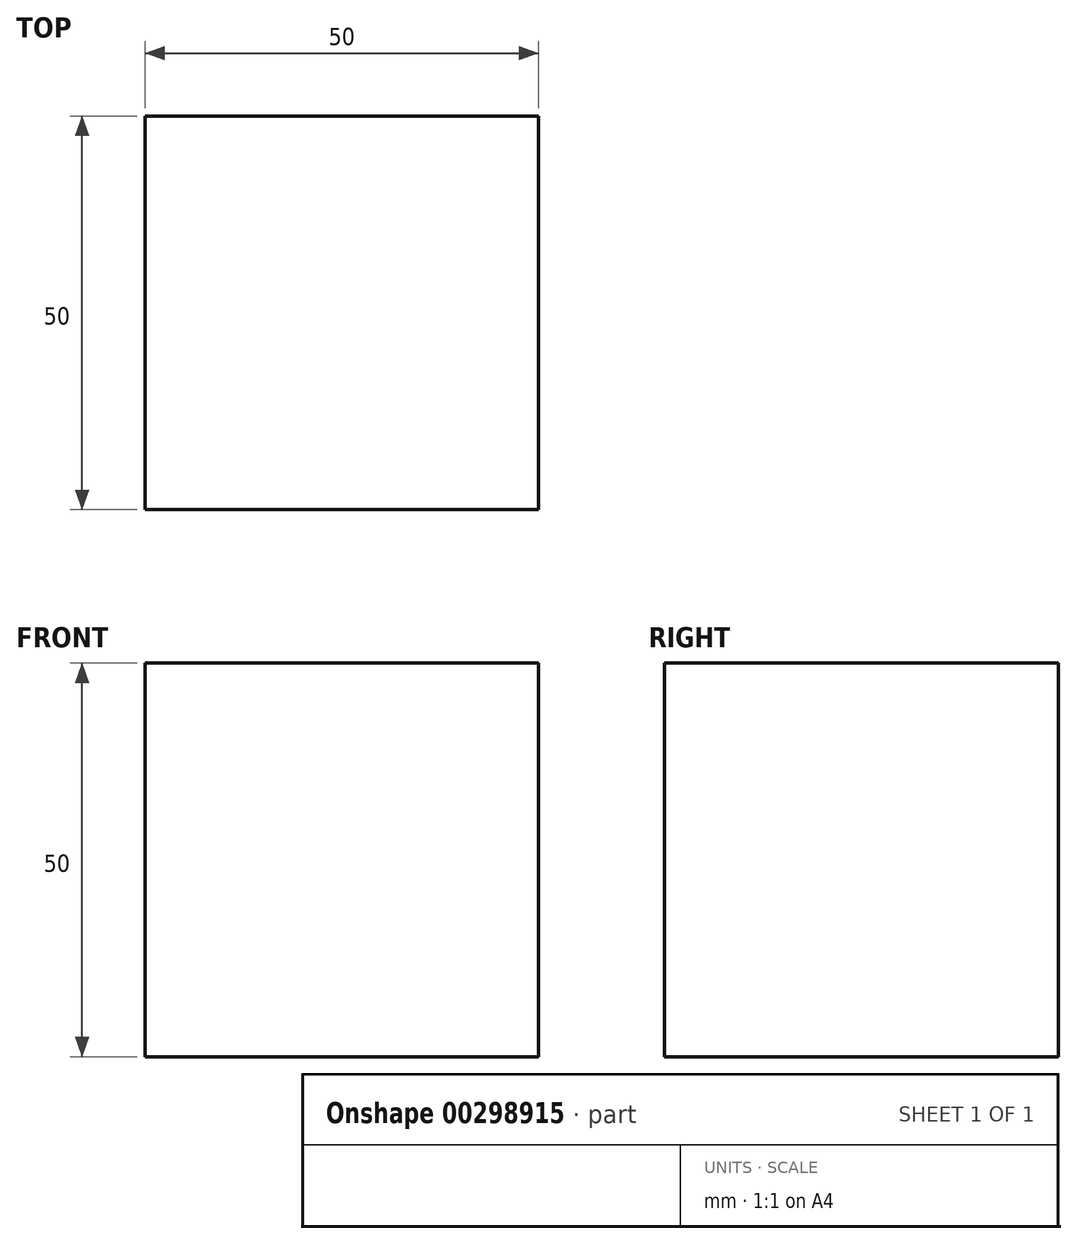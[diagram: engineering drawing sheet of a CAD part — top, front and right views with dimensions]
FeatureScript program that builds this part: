
annotation { "Feature Type Name" : "Feature", "Feature Type Description" : "" }
export const myFeature = defineFeature(function(context is Context, id is Id, definition is map)
    precondition{}
    {
        {
            var Q0;
            Q0=qCreatedBy(makeId("Top.planeOp"),FACE);
            var sketch = newSketch(context, id + "F0", { "sketchPlane" : qUnion([Q0])});
            skLineSegment(sketch, "E0.bottom", {"start": v(25, 25) * mm, "end": v(-25, 25) * mm});
            skLineSegment(sketch, "E0.top", {"start": v(25, -25) * mm, "end": v(-25, -25) * mm});
            skLineSegment(sketch, "E0.left", {"start": v(25, 25) * mm, "end": v(25, -25) * mm});
            skLineSegment(sketch, "E0.right", {"start": v(-25, 25) * mm, "end": v(-25, -25) * mm});
            skPoint(sketch, "E0.middle", {"position": v(0, 0) * mm});
            skSolve(sketch);
        }
        {
            var Q0;
            Q0=makeQuery(id+"F0.imprint","IMPRINT",FACE,{"disambiguationData":[TD([[makeQuery(id+"F0.imprint","IMPRINT",EDGE,{"derivedFrom":sQuery(id+"F0.wireOp",EDGE,"E0.bottom")}),1.0]])]});
            extrude(context, id + "F1", {"entities" : qUnion([Q0]), "depth" : 50 * mm});
        }
    });
